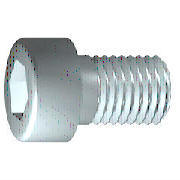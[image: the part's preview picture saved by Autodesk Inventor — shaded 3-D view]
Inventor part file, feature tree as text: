
AUTODESK INVENTOR PART (.ipt)
format: ipt  version: 2017 (Build 210142000, 142)  size: 191,488 bytes
history: native  units: mm (DEFAULTED — no unit token found)
features: sketch x2, extrude x1, plane x1, fillet x1
ambient origin geometry x7: Origin, YZ Plane, XY Plane, X Axis, Y Axis, Z Axis, Center Point
bodies: Solid1 (feature_tree), Body (feature_tree)
feature tree (5):
  extrude  "Slot"  Depth=5.0mm
  plane  "Work Plane1"
  fillet  "Fillet2"  Radius=5.0mm
  sketch  "Sketch1"  dims[d1=13.90924mm d2=0.49086mm d3=5.0mm]
  sketch  "Sketch2"  dims[d4=2.5mm d5=60.0deg d6=5.0mm d7=5.0mm d8=4.618802mm d9=8.5mm d10=90.0deg d11=10.0mm d12=0.0mm d13=13.90924mm d14=0.0mm d15=0.49076mm d16=0.49076mm d17=0.5mm d19=0.0mm d26=16.0mm d27=45.0deg d28=0.0mm d29=0.0mm d30=0.1mm]
